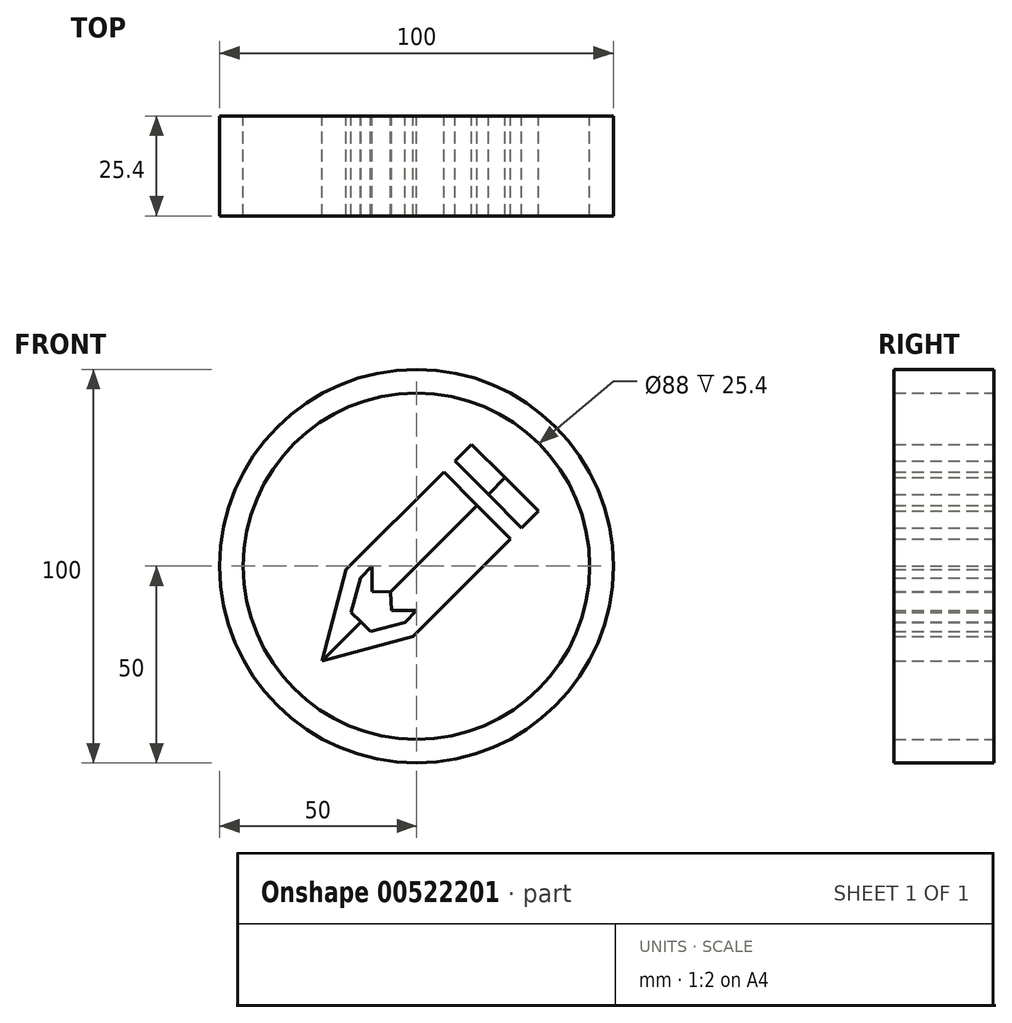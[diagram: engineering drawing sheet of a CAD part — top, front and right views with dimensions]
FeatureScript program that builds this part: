
annotation { "Feature Type Name" : "Feature", "Feature Type Description" : "" }
export const myFeature = defineFeature(function(context is Context, id is Id, definition is map)
    precondition{}
    {
        {
            var Q0;
            Q0=qCreatedBy(makeId("Front.planeOp"),FACE);
            var sketch = newSketch(context, id + "F0", { "sketchPlane" : qUnion([Q0])});
            skCircle(sketch, "E0", {"center": v(0, 0) * mm, "radius": 50 * mm});
            skCircle(sketch, "E1", {"center": v(0, 0) * mm, "radius": 44 * mm});
            skPoint(sketch, "E2", {"position": v(0, -50) * mm});
            skLineSegment(sketch, "E3", {"start": v(0, 0) * mm, "end": v(15.42, 15.42) * mm});
            skLineSegment(sketch, "E4", {"start": v(0, 0) * mm, "end": v(5.25, 0) * mm});
            skLineSegment(sketch, "E5", {"start": v(15.42, 15.42) * mm, "end": v(6.93, 23.9) * mm});
            skLineSegment(sketch, "E6", {"start": v(6.93, 23.9) * mm, "end": v(-17.83, -0.86) * mm});
            skLineSegment(sketch, "E7", {"start": v(0, 0) * mm, "end": v(-24.04, -24.04) * mm});
            skLineSegment(sketch, "E8", {"start": v(-24.04, -24.04) * mm, "end": v(-17.83, -0.86) * mm});
            skLineSegment(sketch, "E9", {"start": v(-14.14, -14.14) * mm, "end": v(-19.86, -8.43) * mm});
            skLineSegment(sketch, "E10.0", {"start": v(9.76, 21.07) * mm, "end": v(-14.24, -2.93) * mm});
            skLineSegment(sketch, "E11.0", {"start": v(-18.38, -18.38) * mm, "end": v(-14.24, -2.93) * mm});
            skLineSegment(sketch, "E12", {"start": v(6.93, 23.9) * mm, "end": v(9.76, 26.73) * mm});
            skLineSegment(sketch, "E13", {"start": v(9.76, 26.73) * mm, "end": v(18.25, 18.25) * mm});
            skLineSegment(sketch, "E14", {"start": v(18.25, 18.25) * mm, "end": v(22.49, 22.49) * mm});
            skLineSegment(sketch, "E15", {"start": v(22.49, 22.49) * mm, "end": v(14, 30.97) * mm});
            skLineSegment(sketch, "E16", {"start": v(14, 30.97) * mm, "end": v(9.76, 26.73) * mm});
            skLineSegment(sketch, "E17", {"start": v(-11.25, 0.07) * mm, "end": v(-11.25, -6.36) * mm});
            skLineSegment(sketch, "E18", {"start": v(-11.25, -6.36) * mm, "end": v(-6.57, -6.57) * mm});
            skSolve(sketch);
        }
        {
            var Q0;
            Q0=makeQuery(id+"F0.imprint","IMPRINT",FACE,{"disambiguationData":[TD([[makeQuery(id+"F0.imprint","IMPRINT",EDGE,{"derivedFrom":sQuery(id+"F0.wireOp",EDGE,"E0")}),1.0]])]});
            var Q1;
            {var subQ9=sQuery(id+"F0.wireOp",EDGE,"JPuuaeZV-5oA1-bOET-emPB-8E9oC848Bjk7");Q1=makeQuery(id+"F0.imprint","IMPRINT",FACE,{"disambiguationData":[TD([[makeQuery(id+"F0.imprint","IMPRINT",EDGE,{"derivedFrom":subQ9}),1.0]])]});}
            var Q2;
            {var subQ1=sQuery(id+"F0.wireOp",EDGE,"1czAJEjm-GAaO-qJbW-bNPJ-VOC9MhbBWLXS");var subQ3=sQuery(id+"F0.wireOp",EDGE,"90a05c53-9c47-40ab-b859-f5c182912d02.1");var subQ4=makeQuery(id+"F0.imprint","INTERSECT",VERTEX,{"derivedFrom":[subQ1,subQ3]});Q2=makeQuery(id+"F0.imprint","IMPRINT",FACE,{"disambiguationData":[TD([[makeQuery(id+"F0.imprint","IMPRINT",EDGE,{"disambiguationData":[TD([[subQ4,-1.0]])],"derivedFrom":subQ3}),1.0]])]});}
            extrude(context, id + "F1", {"entities" : qUnion([Q0, Q1, Q2]), "depth" : 25.4 * mm});
        }
        {
            var Q0;
            {var subQ0=sQuery(id+"F0.wireOp",EDGE,"E8");var subQ1=sQuery(id+"F0.wireOp",EDGE,"E7");var subQ2=makeQuery(id+"F0.imprint","INTERSECT",VERTEX,{"derivedFrom":[subQ1,subQ0]});Q0=makeQuery(id+"F0.imprint","IMPRINT",FACE,{"disambiguationData":[TD([[makeQuery(id+"F0.imprint","IMPRINT",EDGE,{"disambiguationData":[TD([[subQ2,1.0]])],"derivedFrom":subQ1}),-1.0]])]});}
            var Q1;
            {var subQ0=sQuery(id+"F0.wireOp",EDGE,"E9");var subQ1=sQuery(id+"F0.wireOp",EDGE,"E7");var subQ2=makeQuery(id+"F0.imprint","INTERSECT",VERTEX,{"derivedFrom":[subQ1,subQ0]});Q1=makeQuery(id+"F0.imprint","IMPRINT",FACE,{"disambiguationData":[TD([[makeQuery(id+"F0.imprint","IMPRINT",EDGE,{"disambiguationData":[TD([[subQ2,-1.0]])],"derivedFrom":subQ1}),-1.0]])]});}
            var Q2;
            {var subQ5=sQuery(id+"F0.wireOp",EDGE,"E6");Q2=makeQuery(id+"F0.imprint","IMPRINT",FACE,{"disambiguationData":[TD([[makeQuery(id+"F0.imprint","IMPRINT",EDGE,{"derivedFrom":subQ5}),1.0]])]});}
            var Q3;
            {var subQ2=sQuery(id+"F0.wireOp",EDGE,"E3");Q3=makeQuery(id+"F0.imprint","IMPRINT",FACE,{"disambiguationData":[TD([[makeQuery(id+"F0.imprint","IMPRINT",EDGE,{"derivedFrom":subQ2}),1.0]])]});}
            var Q4;
            Q4=makeQuery(id+"F0.imprint","IMPRINT",FACE,{"disambiguationData":[TD([[makeQuery(id+"F0.imprint","IMPRINT",EDGE,{"derivedFrom":sQuery(id+"F0.wireOp",EDGE,"E13")}),1.0]])]});
            extrude(context, id + "F2", {"entities" : qUnion([Q0, Q1, Q2, Q3, Q4]), "depth" : 25.4 * mm, "offsetDistance" : 25.4 * mm});
        }
        {
            var Q0;
            Q0=makeQuery(id+"F2.opExtrude","SWEPT_BODY",BODY,{"disambiguationData":[OSD([sQuery(id+"F0.wireOp",EDGE,"E3"),sQuery(id+"F0.wireOp",EDGE,"E5"),sQuery(id+"F0.wireOp",EDGE,"E6"),sQuery(id+"F0.wireOp",EDGE,"E7"),sQuery(id+"F0.wireOp",EDGE,"E8"),sQuery(id+"F0.wireOp",EDGE,"E9"),sQuery(id+"F0.wireOp",EDGE,"E11.0"),sQuery(id+"F0.wireOp",EDGE,"N8N57HrF-E5I3-f729-v6i4-AL5ZlbmRXCgc"),sQuery(id+"F0.wireOp",EDGE,"vHnO5wzR-NpQP-zZD5-rWtA-ErJBMSODLmsr"),sQuery(id+"F0.wireOp",EDGE,"QRp8Vt7U-pupB-RIvA-a42I-bIf0CRnITRVE")])]});
            var Q1;
            Q1=makeQuery(id+"F2.opExtrude","SWEPT_FACE",FACE,{"disambiguationData":[OSD([sQuery(id+"F0.wireOp",EDGE,"E3"),sQuery(id+"F0.wireOp",EDGE,"E7")])]});
            mirror(context, id + "F3", {"operationType" : NewBodyOperationType.ADD, "entities" : qUnion([Q0]), "mirrorPlane" : qUnion([Q1])});
        }
        {
            var Q0;
            Q0=makeQuery(id+"F2.opExtrude","SWEPT_BODY",BODY,{"disambiguationData":[OSD([sQuery(id+"F0.wireOp",EDGE,"E13"),sQuery(id+"F0.wireOp",EDGE,"E14"),sQuery(id+"F0.wireOp",EDGE,"E15"),sQuery(id+"F0.wireOp",EDGE,"E16")])]});
            var Q1;
            Q1=makeQuery(id+"F2.opExtrude","SWEPT_FACE",FACE,{"disambiguationData":[OSD([sQuery(id+"F0.wireOp",EDGE,"E14")])]});
            mirror(context, id + "F4", {"operationType" : NewBodyOperationType.ADD, "entities" : qUnion([Q0]), "mirrorPlane" : qUnion([Q1])});
        }
    });
